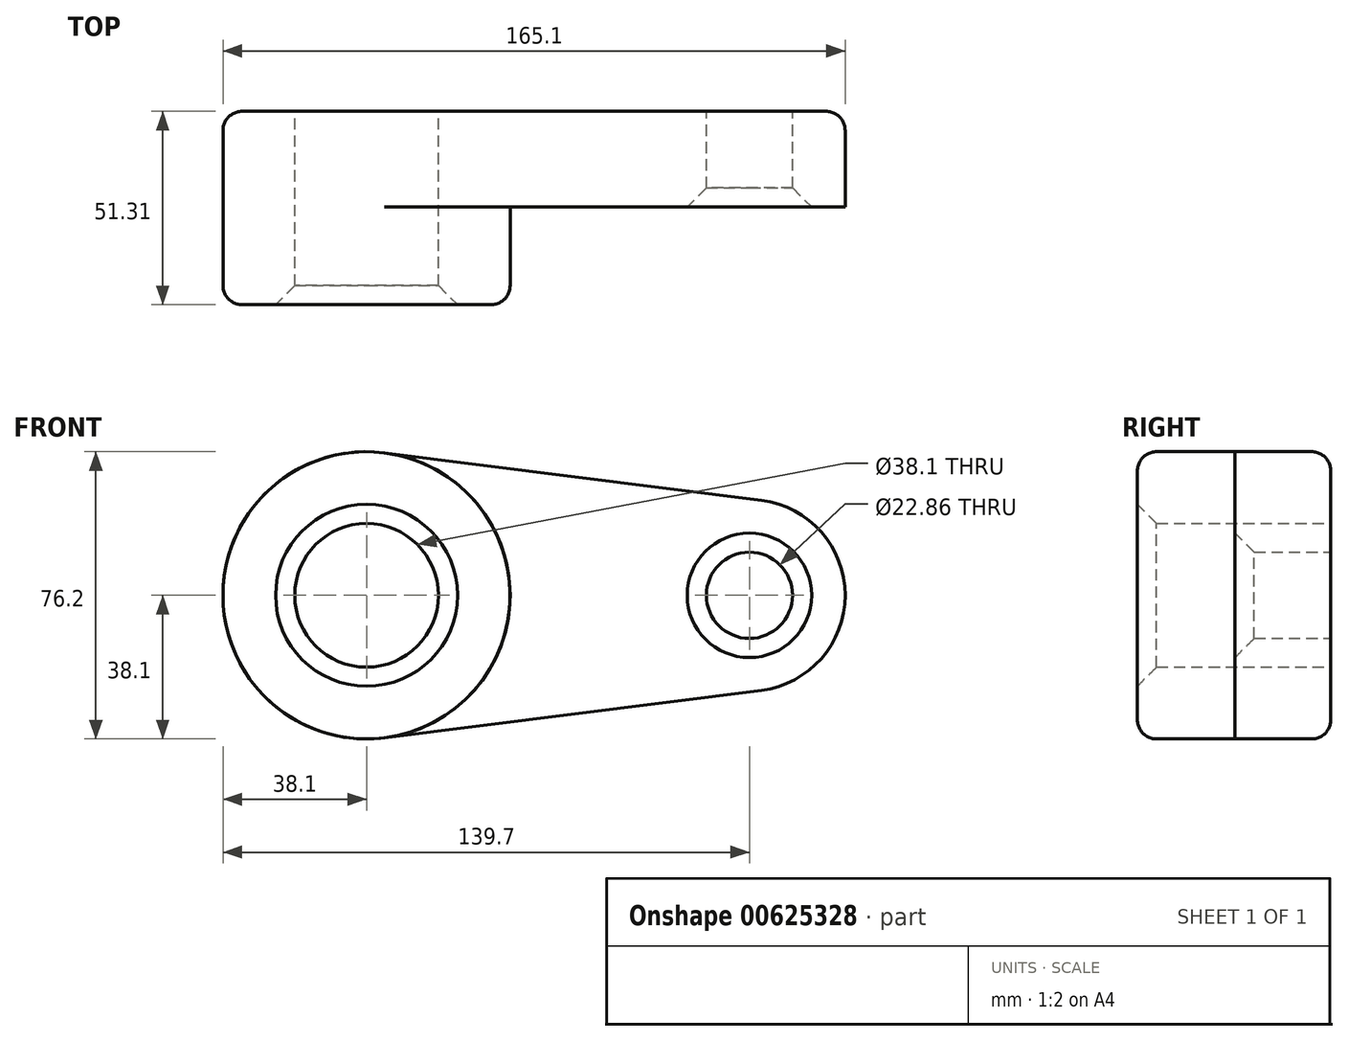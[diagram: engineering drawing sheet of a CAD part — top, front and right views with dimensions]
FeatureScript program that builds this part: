
annotation { "Feature Type Name" : "Feature", "Feature Type Description" : "" }
export const myFeature = defineFeature(function(context is Context, id is Id, definition is map)
    precondition{}
    {
        {
            var Q0;
            Q0=qCreatedBy(makeId("Front.planeOp"),FACE);
            var sketch = newSketch(context, id + "F0", { "sketchPlane" : qUnion([Q0])});
            skCircle(sketch, "E0", {"center": v(0, 0) * mm, "radius": 38.1 * mm});
            skCircle(sketch, "E1", {"center": v(101.6, 0) * mm, "radius": 25.4 * mm});
            skLineSegment(sketch, "E2", {"start": v(4.76, 37.8) * mm, "end": v(104.78, 25.2) * mm});
            skLineSegment(sketch, "E3", {"start": v(4.76, -37.8) * mm, "end": v(104.78, -25.2) * mm});
            skCircle(sketch, "E4", {"center": v(0, 0) * mm, "radius": 19.05 * mm});
            skCircle(sketch, "E5", {"center": v(101.6, 0) * mm, "radius": 11.43 * mm});
            skSolve(sketch);
        }
        {
            var Q0;
            Q0 = qSketchRegion(id + "F0", true);
            extrude(context, id + "F1", {"entities" : qUnion([Q0]), "depth" : 25.4 * mm, "offsetDistance" : 25.4 * mm});
        }
        {
            var Q0;
            Q0=makeQuery(id+"F0.imprint","IMPRINT",FACE,{"disambiguationData":[TD([[makeQuery(id+"F0.imprint","IMPRINT",EDGE,{"derivedFrom":sQuery(id+"F0.wireOp",EDGE,"E4")}),-1.0]])]});
            extrude(context, id + "F2", {"entities" : qUnion([Q0]), "operationType" : NewBodyOperationType.ADD, "depth" : 51.3 * mm, "offsetDistance" : 25.4 * mm});
        }
        {
            var Q0;
            Q0=makeQuery(id+"F2.opExtrude","CAP_EDGE",EDGE,{"disambiguationData":[OSD([sQuery(id+"F0.wireOp",EDGE,"E0")])],"isStart":false});
            var Q1;
            Q1=makeQuery(id+"F1.opExtrude","CAP_EDGE",EDGE,{"disambiguationData":[OSD([sQuery(id+"F0.wireOp",EDGE,"E3")])],"isStart":true});
            fillet(context, id + "F3", {"entities" : qUnion([Q0, Q1]), "radius" : 5.08 * mm, "tangentPropagation" : true, "allowEdgeOverflow" : false});
        }
        {
            var Q0;
            Q0=makeQuery(id+"F2.opExtrude","CAP_EDGE",EDGE,{"disambiguationData":[OSD([sQuery(id+"F0.wireOp",EDGE,"E4")])],"isStart":false});
            var Q1;
            Q1=makeQuery(id+"F1.opExtrude","CAP_EDGE",EDGE,{"disambiguationData":[OSD([sQuery(id+"F0.wireOp",EDGE,"E5")])],"isStart":false});
            chamfer(context, id + "F4", {"entities" : qUnion([Q0, Q1]), "width" : 5.08 * mm, "tangentPropagation" : true});
        }
    });
